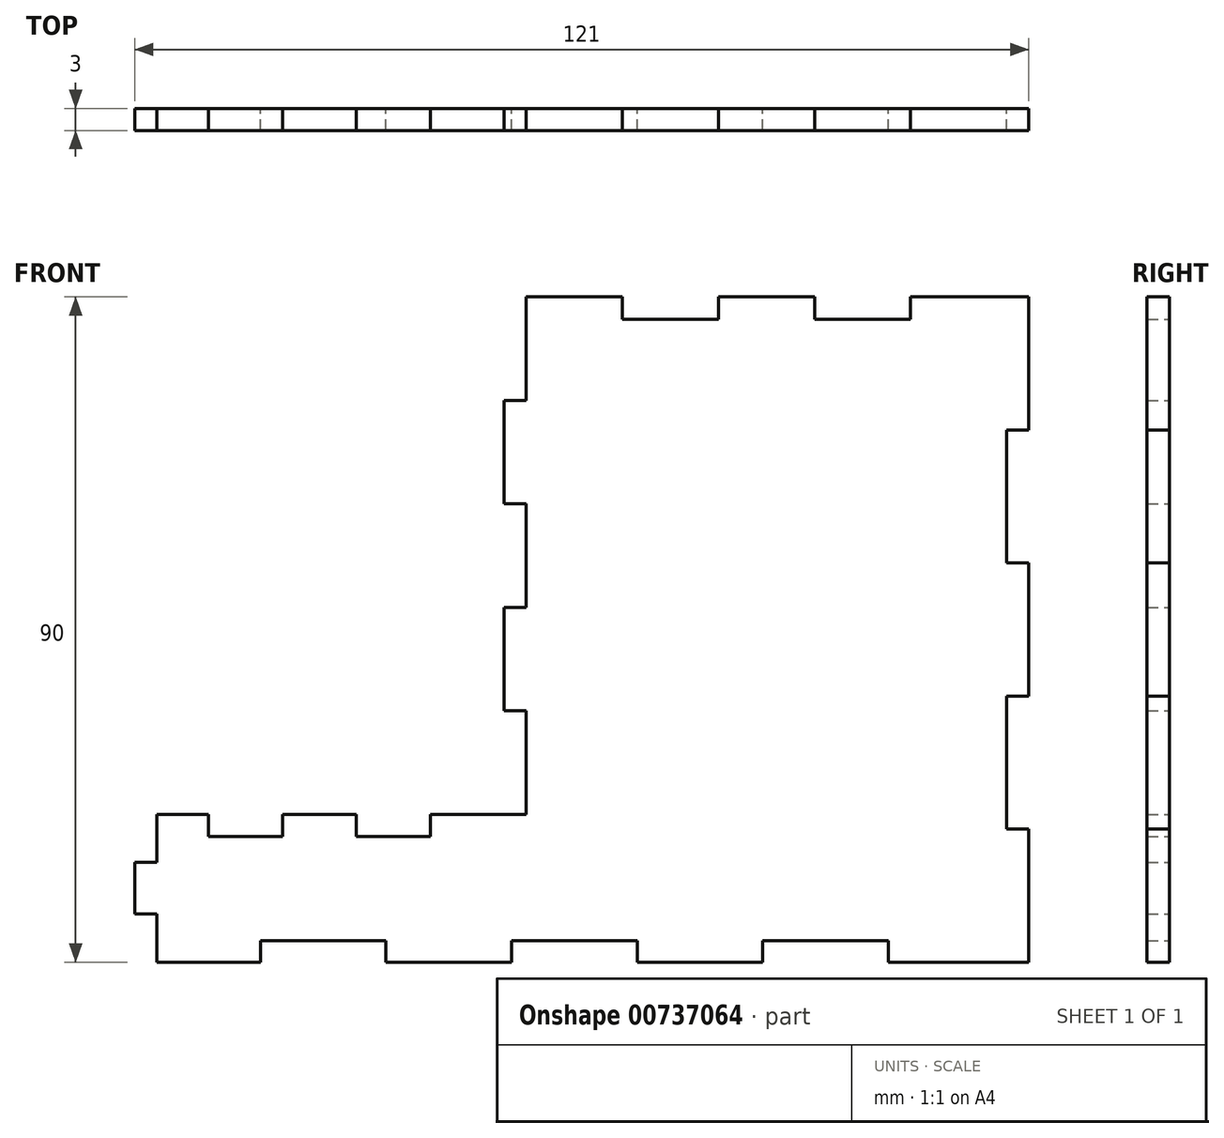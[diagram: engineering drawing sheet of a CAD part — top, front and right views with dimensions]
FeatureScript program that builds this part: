
annotation { "Feature Type Name" : "Feature", "Feature Type Description" : "" }
export const myFeature = defineFeature(function(context is Context, id is Id, definition is map)
    precondition{}
    {
        {
            var Q0;
            Q0=qCreatedBy(makeId("Front.planeOp"),FACE);
            var sketch = newSketch(context, id + "F0", { "sketchPlane" : qUnion([Q0])});
            skLineSegment(sketch, "E0", {"start": v(-50, -34) * mm, "end": v(71, -34) * mm, "construction": true});
            skLineSegment(sketch, "E1", {"start": v(71, -34) * mm, "end": v(71, 56) * mm, "construction": true});
            skLineSegment(sketch, "E2", {"start": v(-50, -14) * mm, "end": v(-50, -34) * mm, "construction": true});
            skLineSegment(sketch, "E3", {"start": v(3, 56) * mm, "end": v(3, 42) * mm});
            skLineSegment(sketch, "E4", {"start": v(3, 42) * mm, "end": v(0, 42) * mm});
            skLineSegment(sketch, "E5", {"start": v(0, 42) * mm, "end": v(0, 28) * mm});
            skLineSegment(sketch, "E6", {"start": v(0, 28) * mm, "end": v(3, 28) * mm});
            skLineSegment(sketch, "E7", {"start": v(3, 28) * mm, "end": v(3, 14) * mm});
            skLineSegment(sketch, "E8", {"start": v(3, 14) * mm, "end": v(0, 14) * mm});
            skLineSegment(sketch, "E9", {"start": v(0, 14) * mm, "end": v(0, 0) * mm});
            skLineSegment(sketch, "E10", {"start": v(0, 0) * mm, "end": v(3, 0) * mm});
            skLineSegment(sketch, "E11", {"start": v(3, 0) * mm, "end": v(3, -14) * mm});
            skLineSegment(sketch, "E12", {"start": v(0, -14) * mm, "end": v(3, -14) * mm});
            skLineSegment(sketch, "E13", {"start": v(3, 56) * mm, "end": v(16, 56) * mm});
            skLineSegment(sketch, "E14", {"start": v(16, 56) * mm, "end": v(16, 53) * mm});
            skLineSegment(sketch, "E15", {"start": v(16, 53) * mm, "end": v(29, 53) * mm});
            skLineSegment(sketch, "E16", {"start": v(29, 53) * mm, "end": v(29, 56) * mm});
            skLineSegment(sketch, "E17", {"start": v(29, 56) * mm, "end": v(42, 56) * mm});
            skLineSegment(sketch, "E18", {"start": v(42, 56) * mm, "end": v(42, 53) * mm});
            skLineSegment(sketch, "E19", {"start": v(42, 53) * mm, "end": v(55, 53) * mm});
            skLineSegment(sketch, "E20", {"start": v(55, 53) * mm, "end": v(55, 56) * mm});
            skLineSegment(sketch, "E21", {"start": v(55, 56) * mm, "end": v(71, 56) * mm});
            skLineSegment(sketch, "E22", {"start": v(71, 56) * mm, "end": v(71, 38) * mm});
            skLineSegment(sketch, "E23", {"start": v(71, 38) * mm, "end": v(68, 38) * mm});
            skLineSegment(sketch, "E24", {"start": v(68, 38) * mm, "end": v(68, 20) * mm});
            skLineSegment(sketch, "E25", {"start": v(68, 20) * mm, "end": v(71, 20) * mm});
            skLineSegment(sketch, "E26", {"start": v(71, 20) * mm, "end": v(71, 2) * mm});
            skLineSegment(sketch, "E27", {"start": v(71, 2) * mm, "end": v(68, 2) * mm});
            skLineSegment(sketch, "E28", {"start": v(68, 2) * mm, "end": v(68, -16) * mm});
            skLineSegment(sketch, "E29", {"start": v(68, -16) * mm, "end": v(71, -16) * mm});
            skLineSegment(sketch, "E30", {"start": v(71, -16) * mm, "end": v(71, -34) * mm});
            skLineSegment(sketch, "E31", {"start": v(-47, -14) * mm, "end": v(-47, -20.5) * mm});
            skLineSegment(sketch, "E32", {"start": v(-47, -20.5) * mm, "end": v(-50, -20.5) * mm});
            skLineSegment(sketch, "E33", {"start": v(-50, -20.5) * mm, "end": v(-50, -27.5) * mm});
            skLineSegment(sketch, "E34", {"start": v(-50, -27.5) * mm, "end": v(-47, -27.5) * mm});
            skLineSegment(sketch, "E35", {"start": v(-47, -27.5) * mm, "end": v(-47, -34) * mm});
            skLineSegment(sketch, "E36", {"start": v(0, 56) * mm, "end": v(0, -14) * mm, "construction": true});
            skLineSegment(sketch, "E37", {"start": v(71, 56) * mm, "end": v(0, 56) * mm, "construction": true});
            skLineSegment(sketch, "E38", {"start": v(0, -14) * mm, "end": v(-50, -14) * mm, "construction": true});
            skLineSegment(sketch, "E39", {"start": v(0, -14) * mm, "end": v(-10, -14) * mm});
            skLineSegment(sketch, "E40", {"start": v(-10, -14) * mm, "end": v(-10, -17) * mm});
            skLineSegment(sketch, "E41", {"start": v(-10, -17) * mm, "end": v(-20, -17) * mm});
            skLineSegment(sketch, "E42", {"start": v(-20, -17) * mm, "end": v(-20, -14) * mm});
            skLineSegment(sketch, "E43", {"start": v(-20, -14) * mm, "end": v(-30, -14) * mm});
            skLineSegment(sketch, "E44", {"start": v(-30, -14) * mm, "end": v(-30, -17) * mm});
            skLineSegment(sketch, "E45", {"start": v(-30, -17) * mm, "end": v(-40, -17) * mm});
            skLineSegment(sketch, "E46", {"start": v(-40, -17) * mm, "end": v(-40, -14) * mm});
            skLineSegment(sketch, "E47", {"start": v(-40, -14) * mm, "end": v(-47, -14) * mm});
            skLineSegment(sketch, "E48", {"start": v(-47, -34) * mm, "end": v(-33, -34) * mm});
            skLineSegment(sketch, "E49", {"start": v(-33, -34) * mm, "end": v(-33, -31.11) * mm});
            skLineSegment(sketch, "E50", {"start": v(-33, -31.11) * mm, "end": v(-16, -31.11) * mm});
            skLineSegment(sketch, "E51", {"start": v(-16, -31.11) * mm, "end": v(-16, -34) * mm});
            skLineSegment(sketch, "E52", {"start": v(-16, -34) * mm, "end": v(1, -34) * mm});
            skLineSegment(sketch, "E53", {"start": v(1, -34) * mm, "end": v(1, -31.11) * mm});
            skLineSegment(sketch, "E54", {"start": v(1, -31.11) * mm, "end": v(18, -31.11) * mm});
            skLineSegment(sketch, "E55", {"start": v(18, -31.11) * mm, "end": v(18, -34) * mm});
            skLineSegment(sketch, "E56", {"start": v(18, -34) * mm, "end": v(35, -34) * mm});
            skLineSegment(sketch, "E57", {"start": v(35, -34) * mm, "end": v(35, -31.11) * mm});
            skLineSegment(sketch, "E58", {"start": v(35, -31.11) * mm, "end": v(52, -31.11) * mm});
            skLineSegment(sketch, "E59", {"start": v(52, -31.11) * mm, "end": v(52, -34) * mm});
            skLineSegment(sketch, "E60", {"start": v(52, -34) * mm, "end": v(71, -34) * mm});
            skSolve(sketch);
        }
        {
            var Q0;
            Q0 = qSketchRegion(id + "F0", true);
            extrude(context, id + "F1", {"entities" : qUnion([Q0]), "depth" : 3 * mm, "offsetDistance" : 25 * mm});
        }
    });
